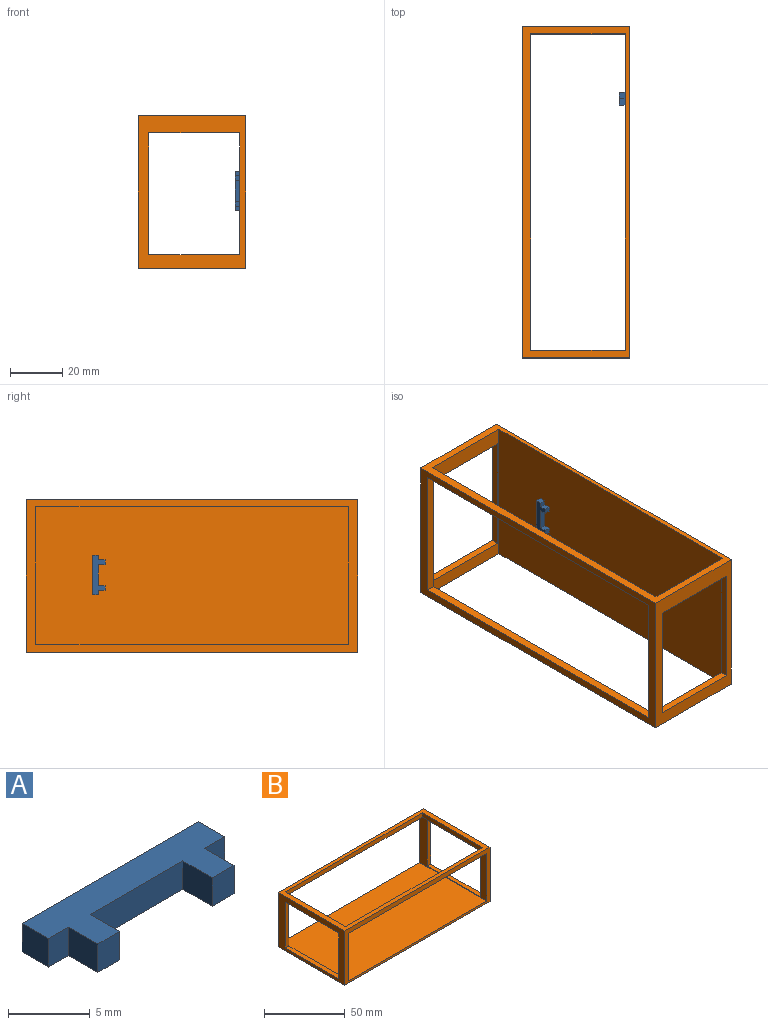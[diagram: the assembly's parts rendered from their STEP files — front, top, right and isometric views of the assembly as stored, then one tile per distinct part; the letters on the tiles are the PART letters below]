
ASSEMBLY  parts=2 mates=2
PART A: 14 faces, bbox 15.2x4.8x2.1 mm
  f0: plane 2.13x1.74mm, normal (0,-1,0), area 3.7mm2, adj f2,f4,f5,f6
  f1: plane 8.02x2.13mm, normal (0,-1,0), area 17mm2, adj f2,f4,f7,f12
  f2: plane 15.24x4.81mm, normal (0,0,-1), area 44.1mm2, adj f0,f1,f3,f5,f6,f7,f8,f9
  f3: plane 15.24x2.13mm, normal (0,1,0), area 32.4mm2, adj f2,f4,f5,f10
  f4: plane 15.24x4.81mm, normal (0,0,1), area 44.1mm2, adj f0,f1,f3,f5,f6,f7,f8,f9
  f5: plane 2.27x2.13mm, normal (-1,0,0), area 4.8mm2, adj f0,f2,f3,f4
  f6: plane 2.54x2.13mm, normal (-1,0,0), area 5.4mm2, adj f0,f2,f4,f8
  f7: plane 2.54x2.13mm, normal (1,0,0), area 5.4mm2, adj f1,f2,f4,f8
  f8: plane 2.13x1.87mm, normal (0,-1,0), area 4mm2, adj f2,f4,f6,f7
  f9: plane 2.13x1.74mm, normal (0,-1,0), area 3.7mm2, adj f2,f4,f10,f11
  f10: plane 2.27x2.13mm, normal (1,0,0), area 4.8mm2, adj f2,f3,f4,f9
  f11: plane 2.54x2.13mm, normal (1,0,0), area 5.4mm2, adj f2,f4,f9,f13
  f12: plane 2.54x2.13mm, normal (-1,0,0), area 5.4mm2, adj f1,f2,f4,f13
  f13: plane 2.13x1.87mm, normal (0,-1,0), area 4mm2, adj f2,f4,f11,f12
PART B: 22 faces, bbox 127x58.4x41.1 mm
  f0: plane 127x58.36mm, normal (0,0,1), area 1110.1mm2, adj f2,f3,f6,f7,f18,f19,f20,f21
  f1: plane 121.02x58.36mm, normal (0,0,-1), area 760.9mm2, adj f4,f5,f6,f7,f18,f19,f20,f21
  f2: plane 58.36x41.06mm, normal (1,0,0), area 772.3mm2, adj f0,f6,f7,f8,f14,f15,f16,f17
  f3: plane 58.36x41.06mm, normal (-1,0,0), area 772.3mm2, adj f0,f6,f7,f8,f10,f11,f12,f13
  f4: plane 58.36x36.01mm, normal (-1,0,0), area 477.4mm2, adj f1,f6,f7,f9,f14,f15,f16,f17
  f5: plane 58.36x36.01mm, normal (1,0,0), area 477.4mm2, adj f1,f6,f7,f9,f10,f11,f12,f13
  f6: plane 127x41.06mm, normal (0,1,0), area 856.9mm2, adj f0,f1,f2,f3,f4,f5,f8,f9
  f7: plane 127x41.06mm, normal (0,-1,0), area 856.9mm2, adj f0,f1,f2,f3,f4,f5,f8,f9
  f8: plane 127x58.36mm, normal (0,0,-1), area 7412.1mm2, adj f2,f3,f6,f7
  f9: plane 121.02x58.36mm, normal (0,0,1), area 7062.9mm2, adj f4,f5,f6,f7
  f10: plane 34.8x3.04mm, normal (0,-1,0), area 105.6mm2, adj f3,f5,f11,f13
  f11: plane 46.68x3.04mm, normal (0,0,1), area 141.7mm2, adj f3,f5,f10,f12
  f12: plane 34.8x3.04mm, normal (0,1,0), area 105.6mm2, adj f3,f5,f11,f13
  f13: plane 46.68x3.04mm, normal (0,0,-1), area 141.7mm2, adj f3,f5,f10,f12
  f14: plane 46.68x2.95mm, normal (0,0,-1), area 137.5mm2, adj f2,f4,f15,f17
  f15: plane 34.8x2.95mm, normal (0,1,0), area 102.5mm2, adj f2,f4,f14,f16
  f16: plane 46.68x2.95mm, normal (0,0,1), area 137.5mm2, adj f2,f4,f15,f17
  f17: plane 34.8x2.95mm, normal (0,-1,0), area 102.5mm2, adj f2,f4,f14,f16
  f18: plane 119.69x3.29mm, normal (0,1,0), area 393.6mm2, adj f0,f1,f19,f21
  f19: plane 52.65x3.29mm, normal (-1,0,0), area 173.1mm2, adj f0,f1,f18,f20
  f20: plane 119.69x3.29mm, normal (0,-1,0), area 393.6mm2, adj f0,f1,f19,f21
  f21: plane 52.65x3.29mm, normal (1,0,0), area 173.1mm2, adj f0,f1,f18,f20
PLACE A rot(axis=(0,-1,0),90deg) t=(59.24,-43.43,5.7)mm
PLACE B rot(axis=(0.58,-0.58,-0.58),120deg) t=(61,-15.76,34.54)mm
MATE planar A.f2 <-> B.f9  axis (1,0,0) through (59.24,-43.43,1.69)mm
MATE parallel B.f3 <-> A.f3  axis (0,1,0) through (38.76,-15.76,6.85)mm
